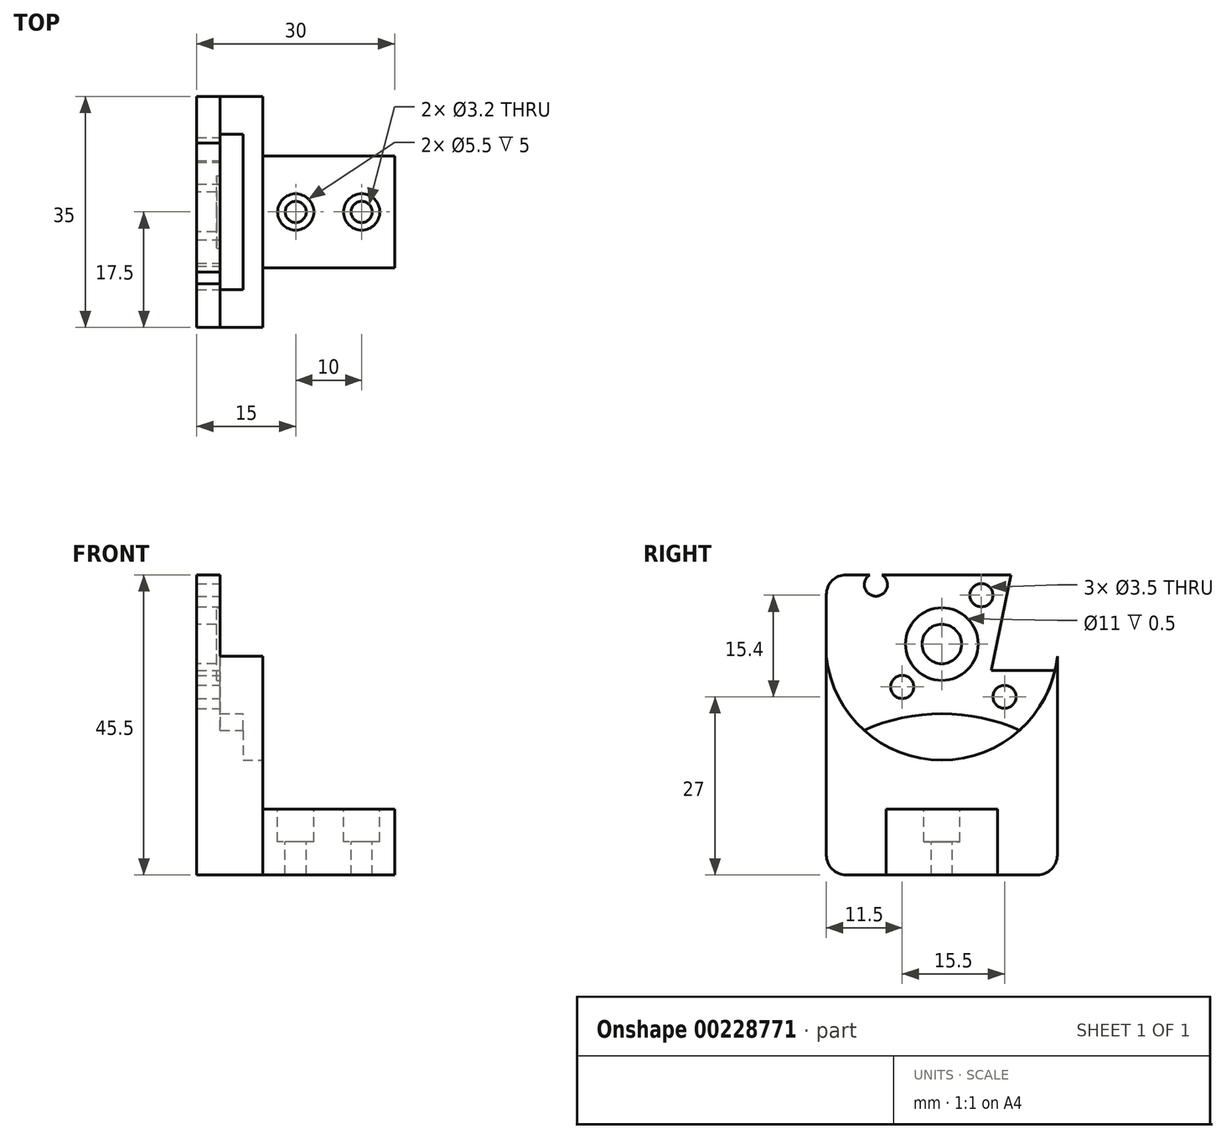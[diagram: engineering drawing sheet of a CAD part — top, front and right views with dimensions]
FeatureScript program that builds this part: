
annotation { "Feature Type Name" : "Feature", "Feature Type Description" : "" }
export const myFeature = defineFeature(function(context is Context, id is Id, definition is map)
    precondition{}
    {
        {
            var Q0;
            Q0=qCreatedBy(makeId("Top.planeOp"),FACE);
            var sketch = newSketch(context, id + "F0", { "sketchPlane" : qUnion([Q0])});
            skLineSegment(sketch, "E0.bottom", {"start": v(-10, 8.45) * mm, "end": v(10, 8.45) * mm});
            skLineSegment(sketch, "E0.top", {"start": v(-10, -8.45) * mm, "end": v(10, -8.45) * mm});
            skLineSegment(sketch, "E0.left", {"start": v(-10, 8.45) * mm, "end": v(-10, -8.45) * mm});
            skLineSegment(sketch, "E0.right", {"start": v(10, 8.45) * mm, "end": v(10, -8.45) * mm});
            skCircle(sketch, "E1", {"center": v(5, 0) * mm, "radius": 1.6 * mm});
            skCircle(sketch, "E2", {"center": v(-5, 0) * mm, "radius": 1.6 * mm});
            skSolve(sketch);
        }
        {
            var Q0;
            Q0=makeQuery(id+"F0.imprint","IMPRINT",FACE,{"disambiguationData":[TD([[makeQuery(id+"F0.imprint","IMPRINT",EDGE,{"derivedFrom":sQuery(id+"F0.wireOp",EDGE,"E0.bottom")}),-1.0]])]});
            extrude(context, id + "F1", {"entities" : qUnion([Q0]), "oppositeDirection" : true, "depth" : 10 * mm});
        }
        {
            var Q0;
            Q0=makeQuery(id+"F1.opExtrude","CAP_FACE",FACE,{"disambiguationData":[OSD([sQuery(id+"F0.wireOp",EDGE,"E0.bottom"),sQuery(id+"F0.wireOp",EDGE,"E0.top"),sQuery(id+"F0.wireOp",EDGE,"E0.left"),sQuery(id+"F0.wireOp",EDGE,"E0.right"),sQuery(id+"F0.wireOp",EDGE,"E1"),sQuery(id+"F0.wireOp",EDGE,"E2")])],"isStart":true});
            var sketch = newSketch(context, id + "F2", { "sketchPlane" : qUnion([Q0])});
            skCircle(sketch, "E3", {"center": v(-5, 0) * mm, "radius": 2.75 * mm});
            skCircle(sketch, "E4", {"center": v(5, 0) * mm, "radius": 2.75 * mm});
            skSolve(sketch);
        }
        {
            var Q0;
            Q0 = qSketchRegion(id + "F2", true);
            extrude(context, id + "F3", {"entities" : qUnion([Q0]), "operationType" : NewBodyOperationType.REMOVE, "oppositeDirection" : true, "depth" : 5 * mm});
        }
        {
            var Q0;
            Q0=makeQuery(id+"F1.opExtrude","SWEPT_FACE",FACE,{"disambiguationData":[OSD([sQuery(id+"F0.wireOp",EDGE,"E0.left")])]});
            var sketch = newSketch(context, id + "F4", { "sketchPlane" : qUnion([Q0])});
            skLineSegment(sketch, "E5.bottom", {"start": v(17.5, -10) * mm, "end": v(-17.5, -10) * mm});
            skLineSegment(sketch, "E5.top", {"start": v(17.5, 35.5) * mm, "end": v(-17.5, 35.5) * mm});
            skLineSegment(sketch, "E5.left", {"start": v(17.5, -10) * mm, "end": v(17.5, 35.5) * mm});
            skLineSegment(sketch, "E5.right", {"start": v(-17.5, -10) * mm, "end": v(-17.5, 35.5) * mm});
            skSolve(sketch);
        }
        {
            var Q0;
            Q0 = qSketchRegion(id + "F4", true);
            extrude(context, id + "F5", {"entities" : qUnion([Q0]), "operationType" : NewBodyOperationType.ADD, "depth" : 10 * mm});
        }
        {
            var Q0;
            Q0=makeQuery(id+"F5.opExtrude","CAP_FACE",FACE,{"disambiguationData":[OSD([sQuery(id+"F4.wireOp",EDGE,"E5.bottom"),sQuery(id+"F4.wireOp",EDGE,"E5.top"),sQuery(id+"F4.wireOp",EDGE,"E5.left"),sQuery(id+"F4.wireOp",EDGE,"E5.right")])],"isStart":false});
            var sketch = newSketch(context, id + "F6", { "sketchPlane" : qUnion([Q0])});
            skCircle(sketch, "E6", {"center": v(0, 25) * mm, "radius": 3 * mm});
            skSolve(sketch);
        }
        {
            var Q0;
            Q0=makeQuery(id+"F6.imprint","IMPRINT",FACE,{"disambiguationData":[TD([[makeQuery(id+"F6.imprint","IMPRINT",EDGE,{"derivedFrom":sQuery(id+"F6.wireOp",EDGE,"E6")}),1.0]])]});
            extrude(context, id + "F7", {"entities" : qUnion([Q0]), "operationType" : NewBodyOperationType.REMOVE, "endBound" : BoundingType.UP_TO_NEXT, "oppositeDirection" : true, "depth" : 25 * mm});
        }
        {
            var Q0;
            Q0=makeQuery(id+"F5.opExtrude","CAP_FACE",FACE,{"disambiguationData":[OSD([sQuery(id+"F4.wireOp",EDGE,"E5.bottom"),sQuery(id+"F4.wireOp",EDGE,"E5.top"),sQuery(id+"F4.wireOp",EDGE,"E5.left"),sQuery(id+"F4.wireOp",EDGE,"E5.right")])],"isStart":true});
            var sketch = newSketch(context, id + "F8", { "sketchPlane" : qUnion([Q0])});
            skArc(sketch, "E7", {"start": v(11.75, 11.9) * mm, "mid": v(16.07, 17.83) * mm, "end": v(17.6, 25) * mm});
            skArc(sketch, "E8", {"start": v(11.8, 11.94) * mm, "mid": v(0, 14.45) * mm, "end": v(-11.8, 11.94) * mm});
            skLineSegment(sketch, "E9", {"start": v(-11.75, 41.56) * mm, "end": v(-11.75, 38.1) * mm, "construction": true});
            skLineSegment(sketch, "E10", {"start": v(11.75, 42.33) * mm, "end": v(11.75, 38.1) * mm, "construction": true});
            skLineSegment(sketch, "E11.trimOffspring", {"start": v(-11.75, 11.96) * mm, "end": v(-11.75, 11.9) * mm, "construction": true});
            skLineSegment(sketch, "E12.trimOffspring", {"start": v(11.75, 11.96) * mm, "end": v(11.75, 11.9) * mm, "construction": true});
            skLineSegment(sketch, "E13", {"start": v(37.13, 25) * mm, "end": v(-35.65, 25) * mm, "construction": true});
            skArc(sketch, "E14.trimOffspring", {"start": v(-17.6, 25) * mm, "mid": v(-16.07, 17.83) * mm, "end": v(-11.75, 11.9) * mm});
            skLineSegment(sketch, "E15", {"start": v(17.6, 25) * mm, "end": v(17.5, 35.5) * mm});
            skLineSegment(sketch, "E16", {"start": v(-17.6, 25) * mm, "end": v(-17.5, 35.5) * mm});
            skLineSegment(sketch, "E17", {"start": v(17.5, 35.5) * mm, "end": v(-17.5, 35.5) * mm});
            skSolve(sketch);
        }
        {
            var Q0;
            {var subQ1=sQuery(id+"F8.wireOp",EDGE,"E8");Q0=makeQuery(id+"F8.imprint","IMPRINT",FACE,{"disambiguationData":[TD([[makeQuery(id+"F8.imprint","IMPRINT",EDGE,{"derivedFrom":subQ1}),-1.0]])]});}
            extrude(context, id + "F9", {"entities" : qUnion([Q0]), "operationType" : NewBodyOperationType.REMOVE, "oppositeDirection" : true, "depth" : 6.5 * mm});
        }
        {
            var Q0;
            {var subQ0=sQuery(id+"F8.wireOp",EDGE,"E8");Q0=makeQuery(id+"F8.imprint","IMPRINT",FACE,{"disambiguationData":[TD([[makeQuery(id+"F8.imprint","IMPRINT",EDGE,{"derivedFrom":subQ0}),1.0]])]});}
            var sketch = newSketch(context, id + "F10", { "sketchPlane" : qUnion([Q0])});
            skCircle(sketch, "E18", {"center": v(6, 32.4) * mm, "radius": 1.75 * mm});
            skCircle(sketch, "E19", {"center": v(9.5, 17) * mm, "radius": 1.75 * mm});
            skCircle(sketch, "E20", {"center": v(-6, 18.5) * mm, "radius": 1.75 * mm});
            skCircle(sketch, "E21", {"center": v(-10, 34) * mm, "radius": 1.75 * mm});
            skSolve(sketch);
        }
        {
            var Q0;
            Q0 = qSketchRegion(id + "F10", true);
            extrude(context, id + "F11", {"entities" : qUnion([Q0]), "operationType" : NewBodyOperationType.REMOVE, "endBound" : BoundingType.THROUGH_ALL, "oppositeDirection" : true, "depth" : 25 * mm});
        }
        {
            var Q0;
            Q0=makeQuery(id+"F9.boolean.opBoolean","COPY",FACE,{"derivedFrom":makeQuery(id+"F9.opExtrude","CAP_FACE",FACE,{"disambiguationData":[OSD([sQuery(id+"F4.wireOp",EDGE,"E5.bottom"),sQuery(id+"F4.wireOp",EDGE,"E5.top"),sQuery(id+"F4.wireOp",EDGE,"E5.left"),sQuery(id+"F4.wireOp",EDGE,"E5.right"),sQuery(id+"F6.wireOp",EDGE,"E6"),sQuery(id+"F8.wireOp",EDGE,"E7"),sQuery(id+"F8.wireOp",EDGE,"E8"),sQuery(id+"F8.wireOp",EDGE,"E14.trimOffspring"),sQuery(id+"F8.wireOp",EDGE,"E15"),sQuery(id+"F8.wireOp",EDGE,"E16"),sQuery(id+"F8.wireOp",EDGE,"E17")])],"isStart":false})});
            var sketch = newSketch(context, id + "F12", { "sketchPlane" : qUnion([Q0])});
            skLineSegment(sketch, "E22.top", {"start": v(17.5, 21) * mm, "end": v(7.5, 21) * mm});
            skLineSegment(sketch, "E22.left", {"start": v(17.5, 35.5) * mm, "end": v(17.5, 21) * mm});
            skLineSegment(sketch, "E23", {"start": v(7.5, 21) * mm, "end": v(10.46, 35.5) * mm});
            skLineSegment(sketch, "E24", {"start": v(17.5, 35.5) * mm, "end": v(10.46, 35.5) * mm});
            skSolve(sketch);
        }
        {
            var Q0;
            Q0 = qSketchRegion(id + "F12", true);
            extrude(context, id + "F13", {"entities" : qUnion([Q0]), "operationType" : NewBodyOperationType.REMOVE, "endBound" : BoundingType.THROUGH_ALL, "oppositeDirection" : true, "depth" : 25 * mm});
        }
        {
            var Q0;
            Q0=makeQuery(id+"F5.opExtrude","CAP_FACE",FACE,{"disambiguationData":[OSD([sQuery(id+"F4.wireOp",EDGE,"E5.bottom"),sQuery(id+"F4.wireOp",EDGE,"E5.top"),sQuery(id+"F4.wireOp",EDGE,"E5.left"),sQuery(id+"F4.wireOp",EDGE,"E5.right")])],"isStart":true});
            var sketch = newSketch(context, id + "F14", { "sketchPlane" : qUnion([Q0])});
            skCircle(sketch, "E25", {"center": v(0, 25) * mm, "radius": 17.6 * mm});
            skSolve(sketch);
        }
        {
            var Q0;
            Q0 = qSketchRegion(id + "F14", true);
            extrude(context, id + "F15", {"entities" : qUnion([Q0]), "operationType" : NewBodyOperationType.REMOVE, "oppositeDirection" : true, "depth" : 3 * mm});
        }
        {
            var Q0;
            Q0=makeQuery(id+"F13.boolean.opBoolean","COPY",EDGE,{"derivedFrom":makeQuery(id+"F13.opExtrude","SWEPT_EDGE",EDGE,{"disambiguationData":[OSD([sQuery(id+"F8.wireOp",EDGE,"E17"),sQuery(id+"F12.wireOp",EDGE,"E23"),sQuery(id+"F12.wireOp",EDGE,"E24")])]})});
            var Q1;
            Q1=makeQuery(id+"F5.opExtrude","SWEPT_EDGE",EDGE,{"disambiguationData":[OSD([sQuery(id+"F4.wireOp",EDGE,"E5.top"),sQuery(id+"F4.wireOp",EDGE,"E5.left")])]});
            var Q2;
            Q2=makeQuery(id+"F5.opExtrude","SWEPT_EDGE",EDGE,{"disambiguationData":[OSD([sQuery(id+"F4.wireOp",EDGE,"E5.bottom"),sQuery(id+"F4.wireOp",EDGE,"E5.left")])]});
            var Q3;
            Q3=makeQuery(id+"F5.opExtrude","SWEPT_EDGE",EDGE,{"disambiguationData":[OSD([sQuery(id+"F4.wireOp",EDGE,"E5.bottom"),sQuery(id+"F4.wireOp",EDGE,"E5.right")])]});
            fillet(context, id + "F16", {"entities" : qUnion([Q0, Q1, Q2, Q3]), "radius" : 3 * mm, "tangentPropagation" : true, "allowEdgeOverflow" : false});
        }
        {
            var Q0;
            Q0=makeQuery(id+"F9.boolean.opBoolean","COPY",FACE,{"derivedFrom":makeQuery(id+"F9.opExtrude","CAP_FACE",FACE,{"disambiguationData":[OSD([sQuery(id+"F4.wireOp",EDGE,"E5.bottom"),sQuery(id+"F4.wireOp",EDGE,"E5.top"),sQuery(id+"F4.wireOp",EDGE,"E5.left"),sQuery(id+"F4.wireOp",EDGE,"E5.right"),sQuery(id+"F6.wireOp",EDGE,"E6"),sQuery(id+"F8.wireOp",EDGE,"E7"),sQuery(id+"F8.wireOp",EDGE,"E8"),sQuery(id+"F8.wireOp",EDGE,"E14.trimOffspring"),sQuery(id+"F8.wireOp",EDGE,"E17")])],"isStart":false})});
            var sketch = newSketch(context, id + "F17", { "sketchPlane" : qUnion([Q0])});
            skCircle(sketch, "E26", {"center": v(0, 25) * mm, "radius": 5.5 * mm});
            skSolve(sketch);
        }
        {
            var Q0;
            Q0 = qSketchRegion(id + "F17", true);
            extrude(context, id + "F18", {"entities" : qUnion([Q0]), "operationType" : NewBodyOperationType.REMOVE, "oppositeDirection" : true, "depth" : 0.5 * mm});
        }
    });
